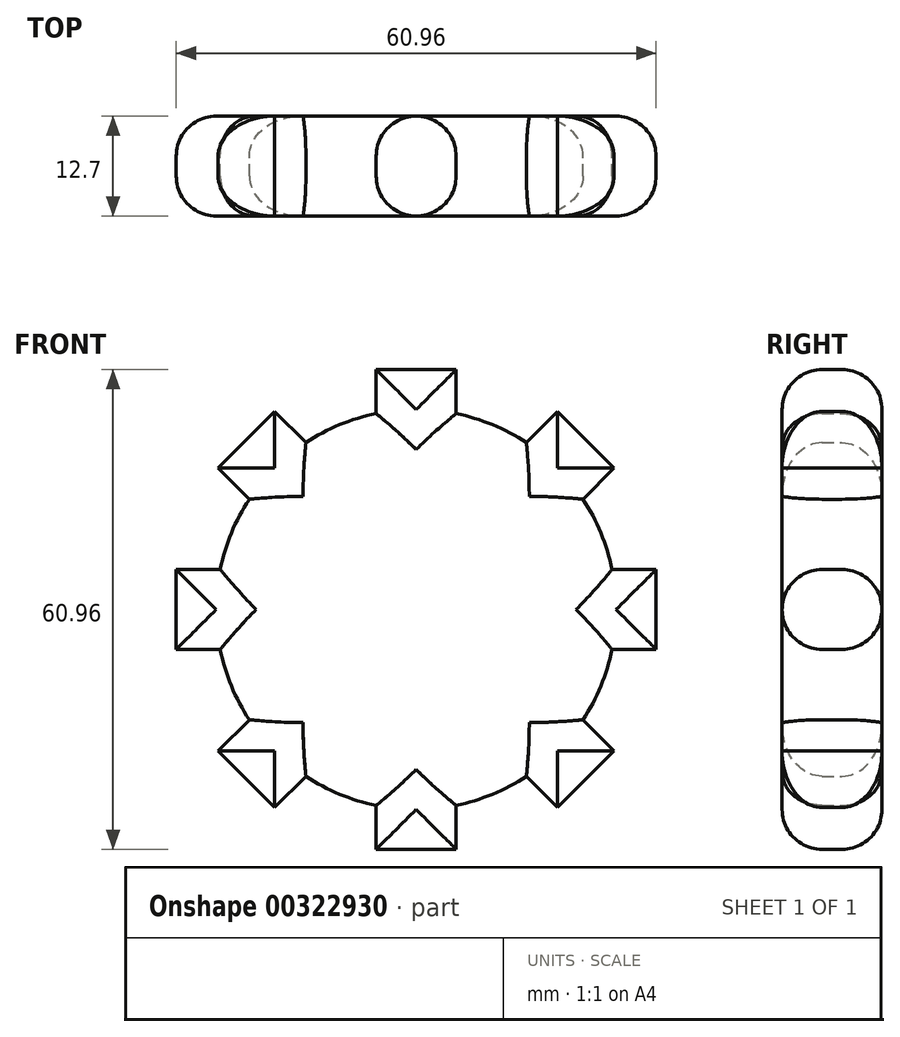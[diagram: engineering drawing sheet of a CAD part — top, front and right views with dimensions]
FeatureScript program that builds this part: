
annotation { "Feature Type Name" : "Feature", "Feature Type Description" : "" }
export const myFeature = defineFeature(function(context is Context, id is Id, definition is map)
    precondition{}
    {
        {
            var Q0;
            Q0=qCreatedBy(makeId("Front.planeOp"),FACE);
            var sketch = newSketch(context, id + "F0", { "sketchPlane" : qUnion([Q0])});
            skCircle(sketch, "E0", {"center": v(0, 0) * mm, "radius": 25.4 * mm});
            skLineSegment(sketch, "E1", {"start": v(0, 30.48) * mm, "end": v(5.08, 30.48) * mm});
            skLineSegment(sketch, "E2", {"start": v(0, 30.48) * mm, "end": v(-5.08, 30.48) * mm});
            skLineSegment(sketch, "E3", {"start": v(-5.08, 30.48) * mm, "end": v(-5.08, 24.89) * mm});
            skLineSegment(sketch, "E4", {"start": v(5.08, 30.48) * mm, "end": v(5.08, 24.89) * mm});
            skLineSegment(sketch, "E5.1.0", {"start": v(-25.14, 17.96) * mm, "end": v(-21.19, 14) * mm});
            skLineSegment(sketch, "E5.1.1", {"start": v(-21.55, 21.55) * mm, "end": v(-25.14, 17.96) * mm});
            skLineSegment(sketch, "E5.1.2", {"start": v(-21.55, 21.55) * mm, "end": v(-17.96, 25.14) * mm});
            skLineSegment(sketch, "E5.1.3", {"start": v(-17.96, 25.14) * mm, "end": v(-14, 21.19) * mm});
            skLineSegment(sketch, "E5.2.0", {"start": v(-30.48, -5.08) * mm, "end": v(-24.89, -5.08) * mm});
            skLineSegment(sketch, "E5.2.1", {"start": v(-30.48, 0) * mm, "end": v(-30.48, -5.08) * mm});
            skLineSegment(sketch, "E5.2.2", {"start": v(-30.48, 0) * mm, "end": v(-30.48, 5.08) * mm});
            skLineSegment(sketch, "E5.2.3", {"start": v(-30.48, 5.08) * mm, "end": v(-24.89, 5.08) * mm});
            skLineSegment(sketch, "E5.3.0", {"start": v(-17.96, -25.14) * mm, "end": v(-14, -21.19) * mm});
            skLineSegment(sketch, "E5.3.1", {"start": v(-21.55, -21.55) * mm, "end": v(-17.96, -25.14) * mm});
            skLineSegment(sketch, "E5.3.2", {"start": v(-21.55, -21.55) * mm, "end": v(-25.14, -17.96) * mm});
            skLineSegment(sketch, "E5.3.3", {"start": v(-25.14, -17.96) * mm, "end": v(-21.19, -14) * mm});
            skLineSegment(sketch, "E5.4.0", {"start": v(5.08, -30.48) * mm, "end": v(5.08, -24.89) * mm});
            skLineSegment(sketch, "E5.4.1", {"start": v(0, -30.48) * mm, "end": v(5.08, -30.48) * mm});
            skLineSegment(sketch, "E5.4.2", {"start": v(0, -30.48) * mm, "end": v(-5.08, -30.48) * mm});
            skLineSegment(sketch, "E5.4.3", {"start": v(-5.08, -30.48) * mm, "end": v(-5.08, -24.89) * mm});
            skLineSegment(sketch, "E5.5.0", {"start": v(25.14, -17.96) * mm, "end": v(21.19, -14) * mm});
            skLineSegment(sketch, "E5.5.1", {"start": v(21.55, -21.55) * mm, "end": v(25.14, -17.96) * mm});
            skLineSegment(sketch, "E5.5.2", {"start": v(21.55, -21.55) * mm, "end": v(17.96, -25.14) * mm});
            skLineSegment(sketch, "E5.5.3", {"start": v(17.96, -25.14) * mm, "end": v(14, -21.19) * mm});
            skLineSegment(sketch, "E5.6.0", {"start": v(30.48, 5.08) * mm, "end": v(24.89, 5.08) * mm});
            skLineSegment(sketch, "E5.6.1", {"start": v(30.48, 0) * mm, "end": v(30.48, 5.08) * mm});
            skLineSegment(sketch, "E5.6.2", {"start": v(30.48, 0) * mm, "end": v(30.48, -5.08) * mm});
            skLineSegment(sketch, "E5.6.3", {"start": v(30.48, -5.08) * mm, "end": v(24.89, -5.08) * mm});
            skLineSegment(sketch, "E5.7.0", {"start": v(17.96, 25.14) * mm, "end": v(14, 21.19) * mm});
            skLineSegment(sketch, "E5.7.1", {"start": v(21.55, 21.55) * mm, "end": v(17.96, 25.14) * mm});
            skLineSegment(sketch, "E5.7.2", {"start": v(21.55, 21.55) * mm, "end": v(25.14, 17.96) * mm});
            skLineSegment(sketch, "E5.7.3", {"start": v(25.14, 17.96) * mm, "end": v(21.19, 14) * mm});
            skSolve(sketch);
        }
        {
            var Q0;
            {var subQ0=sQuery(id+"F0.wireOp",EDGE,"E0");var subQ8=makeQuery(id+"F0.imprint","INTERSECT",VERTEX,{"derivedFrom":[subQ0,sQuery(id+"F0.wireOp",EDGE,"E5.6.0")]});Q0=makeQuery(id+"F0.imprint","IMPRINT",FACE,{"disambiguationData":[TD([[makeQuery(id+"F0.imprint","IMPRINT",EDGE,{"disambiguationData":[TD([[subQ8,-1.0]])],"derivedFrom":subQ0}),1.0]])]});}
            var Q1;
            {var subQ0=sQuery(id+"F0.wireOp",EDGE,"E5.2.0");Q1=makeQuery(id+"F0.imprint","IMPRINT",FACE,{"disambiguationData":[TD([[makeQuery(id+"F0.imprint","IMPRINT",EDGE,{"derivedFrom":subQ0}),1.0]])]});}
            var Q2;
            {var subQ0=sQuery(id+"F0.wireOp",EDGE,"E5.1.0");Q2=makeQuery(id+"F0.imprint","IMPRINT",FACE,{"disambiguationData":[TD([[makeQuery(id+"F0.imprint","IMPRINT",EDGE,{"derivedFrom":subQ0}),1.0]])]});}
            var Q3;
            Q3=makeQuery(id+"F0.imprint","IMPRINT",FACE,{"disambiguationData":[TD([[makeQuery(id+"F0.imprint","IMPRINT",EDGE,{"derivedFrom":sQuery(id+"F0.wireOp",EDGE,"E1")}),-1.0]])]});
            var Q4;
            {var subQ0=sQuery(id+"F0.wireOp",EDGE,"E5.7.0");Q4=makeQuery(id+"F0.imprint","IMPRINT",FACE,{"disambiguationData":[TD([[makeQuery(id+"F0.imprint","IMPRINT",EDGE,{"derivedFrom":subQ0}),1.0]])]});}
            var Q5;
            {var subQ0=sQuery(id+"F0.wireOp",EDGE,"E5.6.0");Q5=makeQuery(id+"F0.imprint","IMPRINT",FACE,{"disambiguationData":[TD([[makeQuery(id+"F0.imprint","IMPRINT",EDGE,{"derivedFrom":subQ0}),1.0]])]});}
            var Q6;
            {var subQ0=sQuery(id+"F0.wireOp",EDGE,"E5.5.0");Q6=makeQuery(id+"F0.imprint","IMPRINT",FACE,{"disambiguationData":[TD([[makeQuery(id+"F0.imprint","IMPRINT",EDGE,{"derivedFrom":subQ0}),1.0]])]});}
            var Q7;
            {var subQ0=sQuery(id+"F0.wireOp",EDGE,"E5.4.0");Q7=makeQuery(id+"F0.imprint","IMPRINT",FACE,{"disambiguationData":[TD([[makeQuery(id+"F0.imprint","IMPRINT",EDGE,{"derivedFrom":subQ0}),1.0]])]});}
            var Q8;
            {var subQ0=sQuery(id+"F0.wireOp",EDGE,"E5.3.0");Q8=makeQuery(id+"F0.imprint","IMPRINT",FACE,{"disambiguationData":[TD([[makeQuery(id+"F0.imprint","IMPRINT",EDGE,{"derivedFrom":subQ0}),1.0]])]});}
            extrude(context, id + "F1", {"entities" : qUnion([Q0, Q1, Q2, Q3, Q4, Q5, Q6, Q7, Q8]), "depth" : 12.7 * mm});
        }
        {
            var Q0;
            Q0=makeQuery(id+"F1.opExtrude","CAP_FACE",FACE,{"disambiguationData":[OSD([sQuery(id+"F0.wireOp",EDGE,"E0"),sQuery(id+"F0.wireOp",EDGE,"E1"),sQuery(id+"F0.wireOp",EDGE,"E2"),sQuery(id+"F0.wireOp",EDGE,"E3"),sQuery(id+"F0.wireOp",EDGE,"E4"),sQuery(id+"F0.wireOp",EDGE,"E5.1.0"),sQuery(id+"F0.wireOp",EDGE,"E5.1.1"),sQuery(id+"F0.wireOp",EDGE,"E5.1.2"),sQuery(id+"F0.wireOp",EDGE,"E5.1.3"),sQuery(id+"F0.wireOp",EDGE,"E5.2.0"),sQuery(id+"F0.wireOp",EDGE,"E5.2.1"),sQuery(id+"F0.wireOp",EDGE,"E5.2.2"),sQuery(id+"F0.wireOp",EDGE,"E5.2.3"),sQuery(id+"F0.wireOp",EDGE,"E5.3.0"),sQuery(id+"F0.wireOp",EDGE,"E5.3.1"),sQuery(id+"F0.wireOp",EDGE,"E5.3.2"),sQuery(id+"F0.wireOp",EDGE,"E5.3.3"),sQuery(id+"F0.wireOp",EDGE,"E5.4.0"),sQuery(id+"F0.wireOp",EDGE,"E5.4.1"),sQuery(id+"F0.wireOp",EDGE,"E5.4.2"),sQuery(id+"F0.wireOp",EDGE,"E5.4.3"),sQuery(id+"F0.wireOp",EDGE,"E5.5.0"),sQuery(id+"F0.wireOp",EDGE,"E5.5.1"),sQuery(id+"F0.wireOp",EDGE,"E5.5.2"),sQuery(id+"F0.wireOp",EDGE,"E5.5.3"),sQuery(id+"F0.wireOp",EDGE,"E5.6.0"),sQuery(id+"F0.wireOp",EDGE,"E5.6.1"),sQuery(id+"F0.wireOp",EDGE,"E5.6.2"),sQuery(id+"F0.wireOp",EDGE,"E5.6.3"),sQuery(id+"F0.wireOp",EDGE,"E5.7.0"),sQuery(id+"F0.wireOp",EDGE,"E5.7.1"),sQuery(id+"F0.wireOp",EDGE,"E5.7.2"),sQuery(id+"F0.wireOp",EDGE,"E5.7.3")])],"isStart":false});
            var Q1;
            Q1=makeQuery(id+"F1.opExtrude","CAP_FACE",FACE,{"disambiguationData":[OSD([sQuery(id+"F0.wireOp",EDGE,"E0"),sQuery(id+"F0.wireOp",EDGE,"E1"),sQuery(id+"F0.wireOp",EDGE,"E2"),sQuery(id+"F0.wireOp",EDGE,"E3"),sQuery(id+"F0.wireOp",EDGE,"E4"),sQuery(id+"F0.wireOp",EDGE,"E5.1.0"),sQuery(id+"F0.wireOp",EDGE,"E5.1.1"),sQuery(id+"F0.wireOp",EDGE,"E5.1.2"),sQuery(id+"F0.wireOp",EDGE,"E5.1.3"),sQuery(id+"F0.wireOp",EDGE,"E5.2.0"),sQuery(id+"F0.wireOp",EDGE,"E5.2.1"),sQuery(id+"F0.wireOp",EDGE,"E5.2.2"),sQuery(id+"F0.wireOp",EDGE,"E5.2.3"),sQuery(id+"F0.wireOp",EDGE,"E5.3.0"),sQuery(id+"F0.wireOp",EDGE,"E5.3.1"),sQuery(id+"F0.wireOp",EDGE,"E5.3.2"),sQuery(id+"F0.wireOp",EDGE,"E5.3.3"),sQuery(id+"F0.wireOp",EDGE,"E5.4.0"),sQuery(id+"F0.wireOp",EDGE,"E5.4.1"),sQuery(id+"F0.wireOp",EDGE,"E5.4.2"),sQuery(id+"F0.wireOp",EDGE,"E5.4.3"),sQuery(id+"F0.wireOp",EDGE,"E5.5.0"),sQuery(id+"F0.wireOp",EDGE,"E5.5.1"),sQuery(id+"F0.wireOp",EDGE,"E5.5.2"),sQuery(id+"F0.wireOp",EDGE,"E5.5.3"),sQuery(id+"F0.wireOp",EDGE,"E5.6.0"),sQuery(id+"F0.wireOp",EDGE,"E5.6.1"),sQuery(id+"F0.wireOp",EDGE,"E5.6.2"),sQuery(id+"F0.wireOp",EDGE,"E5.6.3"),sQuery(id+"F0.wireOp",EDGE,"E5.7.0"),sQuery(id+"F0.wireOp",EDGE,"E5.7.1"),sQuery(id+"F0.wireOp",EDGE,"E5.7.2"),sQuery(id+"F0.wireOp",EDGE,"E5.7.3")])],"isStart":true});
            fillet(context, id + "F2", {"entities" : qUnion([Q0, Q1]), "radius" : 5.08 * mm, "tangentPropagation" : true, "allowEdgeOverflow" : false});
        }
    });
